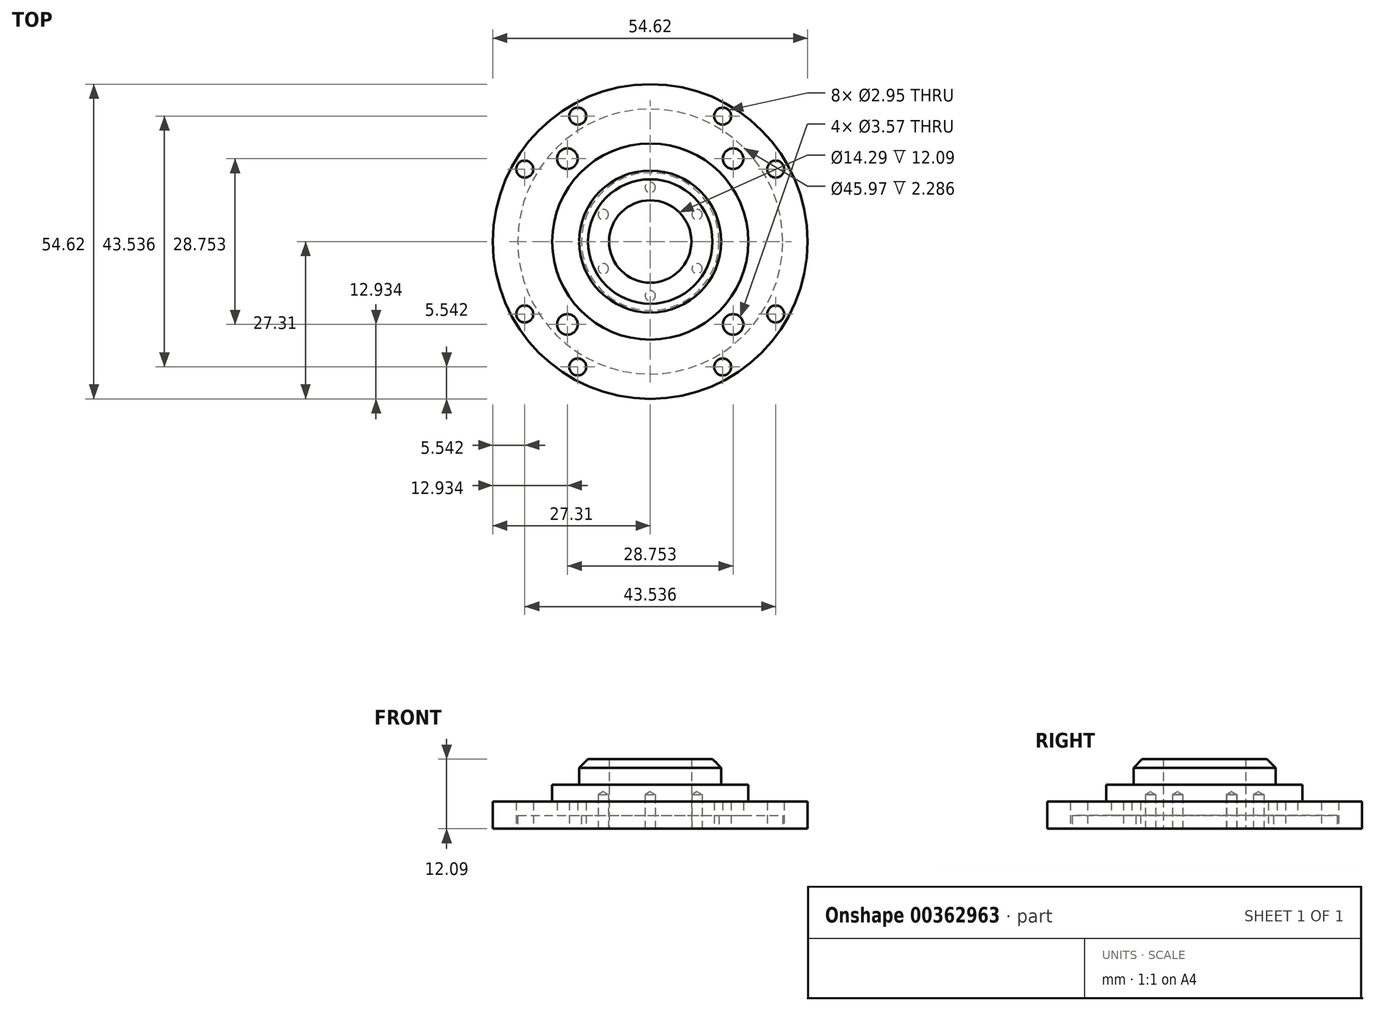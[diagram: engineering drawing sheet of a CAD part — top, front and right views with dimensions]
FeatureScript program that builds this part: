
annotation { "Feature Type Name" : "Feature", "Feature Type Description" : "" }
export const myFeature = defineFeature(function(context is Context, id is Id, definition is map)
    precondition{}
    {
        {
            var Q0;
            Q0=qCreatedBy(makeId("Top.planeOp"),FACE);
            var sketch = newSketch(context, id + "F0", { "sketchPlane" : qUnion([Q0])});
            skCircle(sketch, "E0", {"center": v(0, 0) * mm, "radius": 27.3 * mm});
            skCircle(sketch, "E1", {"center": v(0, 0) * mm, "radius": 7.14 * mm});
            skSolve(sketch);
        }
        {
            var Q0;
            Q0=makeQuery(id+"F0.imprint","IMPRINT",FACE,{"disambiguationData":[TD([[makeQuery(id+"F0.imprint","IMPRINT",EDGE,{"derivedFrom":sQuery(id+"F0.wireOp",EDGE,"E0")}),1.0]])]});
            extrude(context, id + "F1", {"entities" : qUnion([Q0]), "depth" : 4.7 * mm});
        }
        {
            var Q0;
            Q0=makeQuery(id+"F1.opExtrude","CAP_FACE",FACE,{"disambiguationData":[OSD([sQuery(id+"F0.wireOp",EDGE,"E0"),sQuery(id+"F0.wireOp",EDGE,"E1")])],"isStart":false});
            var sketch = newSketch(context, id + "F2", { "sketchPlane" : qUnion([Q0])});
            skCircle(sketch, "E2", {"center": v(0, 0) * mm, "radius": 17.02 * mm});
            skSolve(sketch);
        }
        {
            var Q0;
            Q0=makeQuery(id+"F2.imprint","IMPRINT",FACE,{"disambiguationData":[TD([[makeQuery(id+"F2.imprint","IMPRINT",EDGE,{"derivedFrom":sQuery(id+"F2.wireOp",EDGE,"E2")}),1.0]])]});
            extrude(context, id + "F3", {"entities" : qUnion([Q0]), "operationType" : NewBodyOperationType.ADD, "depth" : 2.92 * mm});
        }
        {
            var Q0;
            Q0=makeQuery(id+"F3.opExtrude","CAP_FACE",FACE,{"disambiguationData":[OSD([sQuery(id+"F0.wireOp",EDGE,"E1"),sQuery(id+"F2.wireOp",EDGE,"E2")])],"isStart":false});
            var sketch = newSketch(context, id + "F4", { "sketchPlane" : qUnion([Q0])});
            skCircle(sketch, "E3", {"center": v(0, 0) * mm, "radius": 12.32 * mm});
            skSolve(sketch);
        }
        {
            var Q0;
            Q0=makeQuery(id+"F4.imprint","IMPRINT",FACE,{"disambiguationData":[TD([[makeQuery(id+"F4.imprint","IMPRINT",EDGE,{"derivedFrom":sQuery(id+"F4.wireOp",EDGE,"E3")}),1.0]])]});
            extrude(context, id + "F5", {"entities" : qUnion([Q0]), "operationType" : NewBodyOperationType.ADD, "depth" : 4.47 * mm});
        }
        {
            var Q0;
            Q0=makeQuery(id+"F5.opExtrude","CAP_EDGE",EDGE,{"disambiguationData":[OSD([sQuery(id+"F4.wireOp",EDGE,"E3")])],"isStart":false});
            chamfer(context, id + "F6", {"entities" : qUnion([Q0]), "chamferType" : ChamferType.OFFSET_ANGLE, "width" : 1.52 * mm, "oppositeDirection" : false, "angle" : 45 * degree, "tangentPropagation" : true});
        }
        {
            var Q0;
            Q0=makeQuery(id+"F1.opExtrude","CAP_FACE",FACE,{"disambiguationData":[OSD([sQuery(id+"F0.wireOp",EDGE,"E0"),sQuery(id+"F0.wireOp",EDGE,"E1")])],"isStart":true});
            var sketch = newSketch(context, id + "F7", { "sketchPlane" : qUnion([Q0])});
            skCircle(sketch, "E4", {"center": v(0, 0) * mm, "radius": 11.94 * mm});
            skCircle(sketch, "E5", {"center": v(0, 0) * mm, "radius": 22.99 * mm});
            skSolve(sketch);
        }
        {
            var Q0;
            Q0=makeQuery(id+"F7.imprint","IMPRINT",FACE,{"disambiguationData":[TD([[makeQuery(id+"F7.imprint","IMPRINT",EDGE,{"derivedFrom":sQuery(id+"F7.wireOp",EDGE,"E4")}),-1.0]])]});
            extrude(context, id + "F8", {"entities" : qUnion([Q0]), "operationType" : NewBodyOperationType.REMOVE, "oppositeDirection" : true, "depth" : 2.3 * mm});
        }
        {
            var Q0;
            {var subQ0=sQuery(id+"F0.wireOp",EDGE,"E0");Q0=makeQuery(id+"F8.boolean.opBoolean","SPLIT",FACE,{"disambiguationData":[TD([makeQuery(id+"F1.opExtrude","SWEPT_FACE",FACE,{"disambiguationData":[OSD([subQ0])]})])],"derivedFrom":makeQuery(id+"F1.opExtrude","CAP_FACE",FACE,{"disambiguationData":[OSD([subQ0,sQuery(id+"F0.wireOp",EDGE,"E1")])],"isStart":true})});}
            var sketch = newSketch(context, id + "F9", { "sketchPlane" : qUnion([Q0])});
            skPoint(sketch, "E6", {"position": v(14.38, 14.38) * mm});
            skPoint(sketch, "E7", {"position": v(0, -9.4) * mm});
            skPoint(sketch, "E8", {"position": v(8.13, -4.7) * mm});
            skPoint(sketch, "E9", {"position": v(12.57, 21.77) * mm});
            skPoint(sketch, "E10", {"position": v(21.77, 12.57) * mm});
            skPoint(sketch, "E11.1.0", {"position": v(-21.77, 12.57) * mm});
            skPoint(sketch, "E11.1.1", {"position": v(-12.57, 21.77) * mm});
            skPoint(sketch, "E11.2.0", {"position": v(-12.57, -21.77) * mm});
            skPoint(sketch, "E11.2.1", {"position": v(-21.77, -12.57) * mm});
            skPoint(sketch, "E11.3.0", {"position": v(21.77, -12.57) * mm});
            skPoint(sketch, "E11.3.1", {"position": v(12.57, -21.77) * mm});
            skPoint(sketch, "E11.center", {"position": v(0, 0) * mm});
            skPoint(sketch, "E12.1.0", {"position": v(-14.38, 14.38) * mm});
            skPoint(sketch, "E12.2.0", {"position": v(-14.38, -14.38) * mm});
            skPoint(sketch, "E12.3.0", {"position": v(14.38, -14.38) * mm});
            skPoint(sketch, "E13.1.0", {"position": v(0, 9.39) * mm});
            skPoint(sketch, "E13.1.1", {"position": v(8.14, 4.7) * mm});
            skPoint(sketch, "E13.2.0", {"position": v(-8.13, -4.69) * mm});
            skPoint(sketch, "E13.2.1", {"position": v(-8.14, 4.7) * mm});
            skSolve(sketch);
        }
        {
            var Q0;
            Q0=sQuery(id+"F9.wireOp",VERTEX,"E13.2.1");
            var Q1;
            Q1=sQuery(id+"F9.wireOp",VERTEX,"E13.2.0");
            var Q2;
            Q2=sQuery(id+"F9.wireOp",VERTEX,"E13.1.1");
            var Q3;
            Q3=sQuery(id+"F9.wireOp",VERTEX,"E11.center");
            var Q4;
            Q4=sQuery(id+"F9.wireOp",VERTEX,"E13.1.0");
            var Q5;
            Q5=sQuery(id+"F9.wireOp",VERTEX,"E7");
            var Q6;
            Q6=sQuery(id+"F9.wireOp",VERTEX,"E8");
            var Q7;
            Q7=makeQuery(id+"F1.opExtrude","SWEPT_BODY",BODY,{"disambiguationData":[OSD([sQuery(id+"F0.wireOp",EDGE,"E0"),sQuery(id+"F0.wireOp",EDGE,"E1")])]});
            hole(context, id + "F10", {"style" : HoleStyle.SIMPLE, "endStyle" : HoleEndStyle.BLIND, "standardTappedOrClearance" : lookupTablePath({ "standard" : "ANSI", "engagement" : "75%", "pitch" : "56 tpi", "size" : "#2", "type" : "Tapped" }), "standardBlindInLast" : lookupTablePath({ "standard" : "ANSI", "engagement" : "75%", "pitch" : "56 tpi", "size" : "#2", "type" : "Tapped" }), "holeDiameter" : 1.78 * mm, "showTappedDepth" : true, "holeDepth" : 5.93 * mm, "isTappedThrough" : true, "tappedDepth" : 4.57 * mm, "tapClearance" : 3, "startFromSketch" : true, "locations" : qUnion([Q0, Q1, Q2, Q3, Q4, Q5, Q6]), "scope" : qUnion([Q7]), "majorDiameter" : 2.18 * mm});
        }
        {
            var Q0;
            Q0=sQuery(id+"F9.wireOp",VERTEX,"E6");
            var Q1;
            Q1=sQuery(id+"F9.wireOp",VERTEX,"E12.3.0");
            var Q2;
            Q2=sQuery(id+"F9.wireOp",VERTEX,"E12.2.0");
            var Q3;
            Q3=sQuery(id+"F9.wireOp",VERTEX,"E12.1.0");
            var Q4;
            Q4=makeQuery(id+"F1.opExtrude","SWEPT_BODY",BODY,{"disambiguationData":[OSD([sQuery(id+"F0.wireOp",EDGE,"E0"),sQuery(id+"F0.wireOp",EDGE,"E1")])]});
            hole(context, id + "F11", {"style" : HoleStyle.SIMPLE, "endStyle" : HoleEndStyle.THROUGH, "standardTappedOrClearance" : lookupTablePath({ "standard" : "ANSI", "size" : "#28 (0.14)", "type" : "Drilled" }), "standardBlindInLast" : lookupTablePath({ "standard" : "ANSI", "size" : "#28", "type" : "Drilled" }), "holeDiameter" : 3.57 * mm, "isTappedThrough" : true, "tappedDepth" : 4.58 * mm, "tapClearance" : 3, "startFromSketch" : true, "locations" : qUnion([Q0, Q1, Q2, Q3]), "scope" : qUnion([Q4])});
        }
        {
            var Q0;
            Q0=sQuery(id+"F9.wireOp",VERTEX,"E9");
            var Q1;
            Q1=sQuery(id+"F9.wireOp",VERTEX,"E10");
            var Q2;
            Q2=sQuery(id+"F9.wireOp",VERTEX,"E11.3.0");
            var Q3;
            Q3=sQuery(id+"F9.wireOp",VERTEX,"E11.3.1");
            var Q4;
            Q4=sQuery(id+"F9.wireOp",VERTEX,"E11.2.0");
            var Q5;
            Q5=sQuery(id+"F9.wireOp",VERTEX,"E11.2.1");
            var Q6;
            Q6=sQuery(id+"F9.wireOp",VERTEX,"E11.1.0");
            var Q7;
            Q7=sQuery(id+"F9.wireOp",VERTEX,"E11.1.1");
            var Q8;
            Q8=makeQuery(id+"F1.opExtrude","SWEPT_BODY",BODY,{"disambiguationData":[OSD([sQuery(id+"F0.wireOp",EDGE,"E0"),sQuery(id+"F0.wireOp",EDGE,"E1")])]});
            hole(context, id + "F12", {"style" : HoleStyle.SIMPLE, "endStyle" : HoleEndStyle.THROUGH, "standardTappedOrClearance" : lookupTablePath({ "standard" : "ANSI", "size" : "#32 (0.12)", "type" : "Drilled" }), "standardBlindInLast" : lookupTablePath({ "standard" : "ANSI", "size" : "#32", "type" : "Drilled" }), "holeDiameter" : 2.95 * mm, "isTappedThrough" : true, "tappedDepth" : 4.57 * mm, "tapClearance" : 3, "startFromSketch" : true, "locations" : qUnion([Q0, Q1, Q2, Q3, Q4, Q5, Q6, Q7]), "scope" : qUnion([Q8])});
        }
    });
